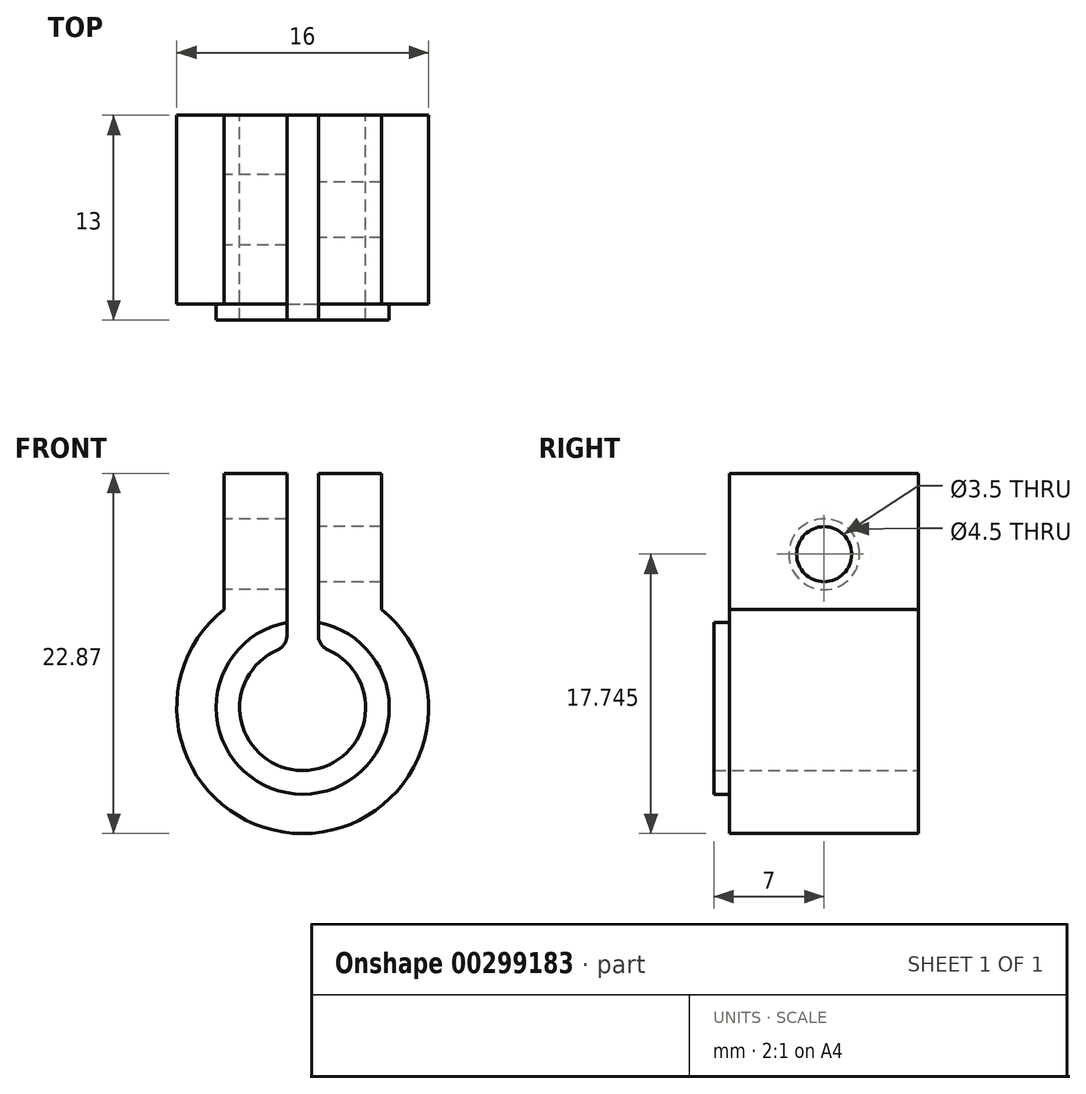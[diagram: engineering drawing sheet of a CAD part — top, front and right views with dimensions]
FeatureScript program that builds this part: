
annotation { "Feature Type Name" : "Feature", "Feature Type Description" : "" }
export const myFeature = defineFeature(function(context is Context, id is Id, definition is map)
    precondition{}
    {
        {
            var Q0;
            Q0=qCreatedBy(makeId("Front.planeOp"),FACE);
            var sketch = newSketch(context, id + "F0", { "sketchPlane" : qUnion([Q0])});
            skArc(sketch, "E0", {"start": v(-1, 3.87) * mm, "mid": v(0, -4) * mm, "end": v(1, 3.87) * mm});
            skArc(sketch, "E1", {"start": v(-5, 6.24) * mm, "mid": v(0, -8) * mm, "end": v(5, 6.24) * mm});
            skLineSegment(sketch, "E2", {"start": v(-1, 14.87) * mm, "end": v(-5, 14.87) * mm});
            skLineSegment(sketch, "E3", {"start": v(-5, 14.87) * mm, "end": v(-5, 6.24) * mm});
            skLineSegment(sketch, "E4", {"start": v(1, 14.87) * mm, "end": v(5, 14.87) * mm});
            skLineSegment(sketch, "E5", {"start": v(5, 14.87) * mm, "end": v(5, 6.24) * mm});
            skLineSegment(sketch, "E6", {"start": v(-1, 3.87) * mm, "end": v(-1, 14.87) * mm});
            skLineSegment(sketch, "E7", {"start": v(1, 14.87) * mm, "end": v(1, 3.87) * mm});
            skSolve(sketch);
        }
        {
            var Q0;
            Q0 = qSketchRegion(id + "F0", true);
            extrude(context, id + "F1", {"entities" : qUnion([Q0]), "depth" : 12 * mm});
        }
        {
            var Q0;
            Q0=makeQuery(id+"F1.opExtrude","CAP_FACE",FACE,{"disambiguationData":[OSD([sQuery(id+"F0.wireOp",EDGE,"E0"),sQuery(id+"F0.wireOp",EDGE,"E1"),sQuery(id+"F0.wireOp",EDGE,"E2"),sQuery(id+"F0.wireOp",EDGE,"E3"),sQuery(id+"F0.wireOp",EDGE,"E4"),sQuery(id+"F0.wireOp",EDGE,"E5"),sQuery(id+"F0.wireOp",EDGE,"E6"),sQuery(id+"F0.wireOp",EDGE,"E7")])],"isStart":false});
            var sketch = newSketch(context, id + "F2", { "sketchPlane" : qUnion([Q0])});
            skArc(sketch, "E8", {"start": v(-1, 3.87) * mm, "mid": v(0, -4) * mm, "end": v(1, 3.87) * mm});
            skArc(sketch, "E9", {"start": v(-1, 5.4) * mm, "mid": v(0, -5.5) * mm, "end": v(1, 5.4) * mm});
            skLineSegment(sketch, "E10", {"start": v(-1, 5.4) * mm, "end": v(-1, 3.87) * mm});
            skLineSegment(sketch, "E11", {"start": v(1, 5.4) * mm, "end": v(1, 3.87) * mm});
            skSolve(sketch);
        }
        {
            var Q0;
            Q0 = qSketchRegion(id + "F2", true);
            extrude(context, id + "F3", {"entities" : qUnion([Q0]), "operationType" : NewBodyOperationType.ADD, "depth" : 1 * mm});
        }
        {
            var Q0;
            Q0=makeQuery(id+"F3.boolean.opBoolean","MERGE",EDGE,{"derivedFrom":[makeQuery(id+"F1.opExtrude","SWEPT_EDGE",EDGE,{"disambiguationData":[OSD([sQuery(id+"F0.wireOp",EDGE,"E0"),sQuery(id+"F0.wireOp",EDGE,"E6")])]}),makeQuery(id+"F3.opExtrude","SWEPT_EDGE",EDGE,{"disambiguationData":[OSD([sQuery(id+"F2.wireOp",EDGE,"E8"),sQuery(id+"F2.wireOp",EDGE,"E10")])]})]});
            var Q1;
            Q1=makeQuery(id+"F3.boolean.opBoolean","MERGE",EDGE,{"derivedFrom":[makeQuery(id+"F1.opExtrude","SWEPT_EDGE",EDGE,{"disambiguationData":[OSD([sQuery(id+"F0.wireOp",EDGE,"E0"),sQuery(id+"F0.wireOp",EDGE,"E7")])]}),makeQuery(id+"F3.opExtrude","SWEPT_EDGE",EDGE,{"disambiguationData":[OSD([sQuery(id+"F2.wireOp",EDGE,"E8"),sQuery(id+"F2.wireOp",EDGE,"E11")])]})]});
            fillet(context, id + "F4", {"entities" : qUnion([Q0, Q1]), "radius" : 1 * mm, "tangentPropagation" : true, "allowEdgeOverflow" : false});
        }
        {
            var Q0;
            Q0=makeQuery(id+"F1.opExtrude","SWEPT_FACE",FACE,{"disambiguationData":[OSD([sQuery(id+"F0.wireOp",EDGE,"E3")])]});
            var sketch = newSketch(context, id + "F5", { "sketchPlane" : qUnion([Q0])});
            skCircle(sketch, "E12", {"center": v(6, 9.74) * mm, "radius": 1.75 * mm});
            skSolve(sketch);
        }
        {
            var Q0;
            Q0 = qSketchRegion(id + "F5", true);
            extrude(context, id + "F6", {"entities" : qUnion([Q0]), "operationType" : NewBodyOperationType.REMOVE, "oppositeDirection" : true, "depth" : 11.8 * mm});
        }
        {
            var Q0;
            Q0=makeQuery(id+"F1.opExtrude","SWEPT_FACE",FACE,{"disambiguationData":[OSD([sQuery(id+"F0.wireOp",EDGE,"E3")])]});
            var sketch = newSketch(context, id + "F7", { "sketchPlane" : qUnion([Q0])});
            skCircle(sketch, "E13", {"center": v(6, 9.74) * mm, "radius": 2.25 * mm});
            skSolve(sketch);
        }
        {
            var Q0;
            Q0 = qSketchRegion(id + "F7", true);
            extrude(context, id + "F8", {"entities" : qUnion([Q0]), "operationType" : NewBodyOperationType.REMOVE, "oppositeDirection" : true, "depth" : 4.8 * mm});
        }
    });
